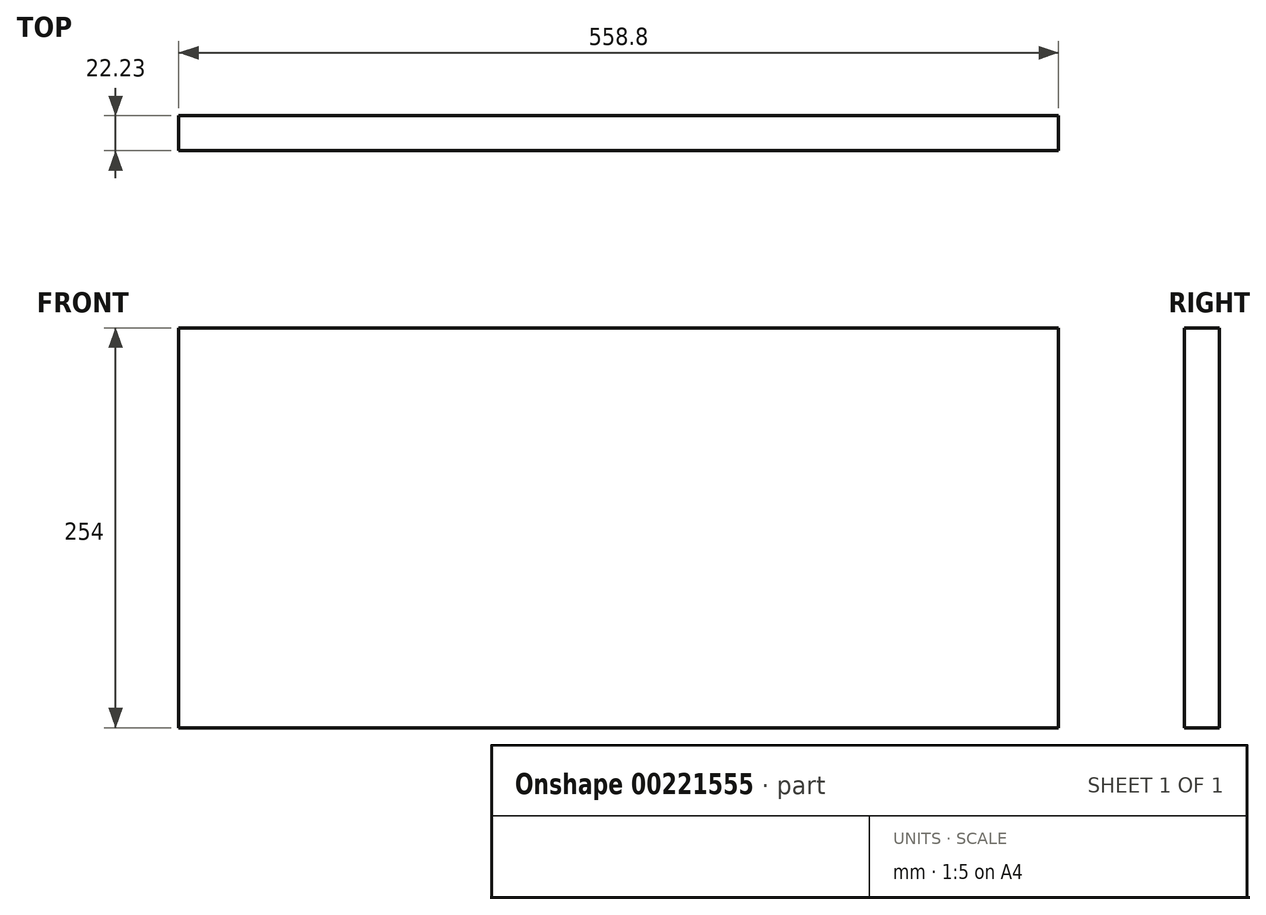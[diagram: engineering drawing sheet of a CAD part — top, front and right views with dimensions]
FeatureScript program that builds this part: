
annotation { "Feature Type Name" : "Feature", "Feature Type Description" : "" }
export const myFeature = defineFeature(function(context is Context, id is Id, definition is map)
    precondition{}
    {
        {
            var Q0;
            Q0=qCreatedBy(makeId("Front.planeOp"),FACE);
            var sketch = newSketch(context, id + "F0", { "sketchPlane" : qUnion([Q0])});
            skLineSegment(sketch, "E0", {"start": v(0, 0) * mm, "end": v(558.8, 0) * mm});
            skLineSegment(sketch, "E1", {"start": v(558.8, 0) * mm, "end": v(558.8, 254) * mm});
            skLineSegment(sketch, "E2", {"start": v(558.8, 254) * mm, "end": v(0, 254) * mm});
            skLineSegment(sketch, "E3", {"start": v(0, 254) * mm, "end": v(0, 0) * mm});
            skSolve(sketch);
        }
        {
            var Q0;
            Q0 = qSketchRegion(id + "F0", true);
            extrude(context, id + "F1", {"entities" : qUnion([Q0]), "depth" : 22.22 * mm});
        }
    });
